# Revit family: Haworth_BelongGallaryEndPanel_Limited
name_source: partatom
category: Furniture Systems
revit_build: Autodesk Revit 2018 (Build: 20170223_1515(x64)
units: mm (PartAtom-declared; Revit-internal decimal feet)

## family parameters
Always vertical = Yes
Cut with Voids When Loaded = No
OmniClass Number = 23.40.70.14.64.21
OmniClass Title = Systems Furniture
Part Type = Normal
Room Calculation Point = No
Round Connector Dimension = Use Diameter
Shared = No
Work Plane-Based = No

## types (3) — shared parameters
Actual Mounting Height = 27 13/16"
Assembly Code = E2020200
Bracket Finish = Haworth _ Paint _ Undecided
Bracket Offset = 4 3/8"
Bracket Width = 1 1/4"
Description = Haworth - Belong Gallary Panel
Manufacturer = Haworth
Max. Height = 50"
Max. Width = 300"
Min. Height = 17"
Min. Width = 24"
Model = Haworth - Belong Gallary Panel
Panel Bottom Offset = 0"
Revision Number = 1
Screen Depth = 1 1/2"
Screen Finish = Haworth _ Laminate _ Undecided _ Panel
Size = Verify Final Dim. w/ Haworth
Sustainability Info = https://www.haworth.com
URL = http://www.haworth.com
URL - Product = http://www.haworth.com
Warranty = http://www.haworth.com
Worksurface Thickness = 1 3/16"

## per-type parameters (varying)
| type | Actual Height | Actual Width | Bracket Spacing | Height | Standard Heights | Standard Widths | Width |
| 42h 144w | 42" | 143 1/2" | 133 1/2" | 42" | 17in. or 25 in. | 23-58 in. | 144" |
| 42h 42w | 42" | 41 1/2" | 31 1/2" | 42" |  |  | 42" |
| 50h 63w | 50" | 62 1/2" | 52 1/2" | 50" | 17in. or 25 in. | 23-58 in. | 63" |

## geometry (parser evidence)
native form markers: Blend x6, Sweep x3
no freeform markers — native parametric forms only
